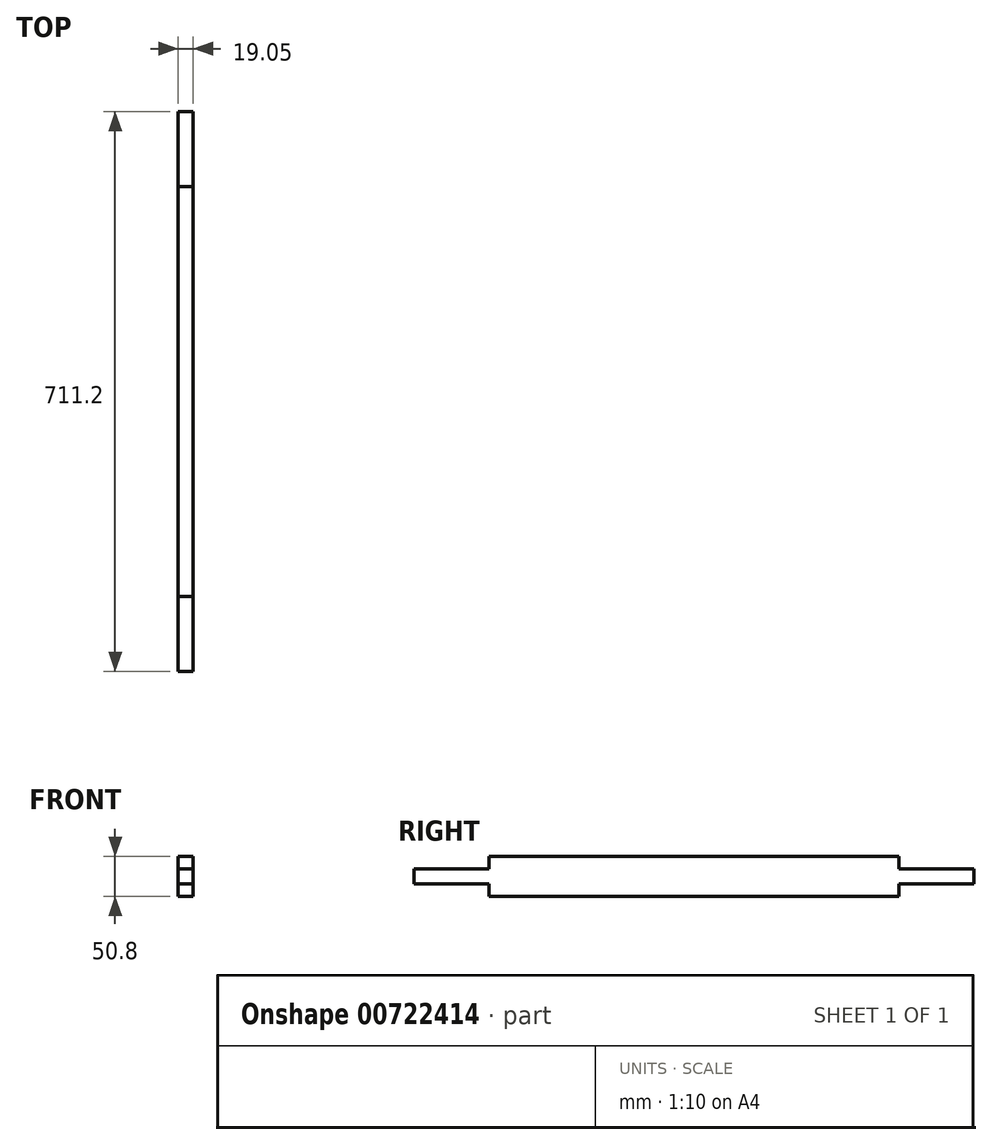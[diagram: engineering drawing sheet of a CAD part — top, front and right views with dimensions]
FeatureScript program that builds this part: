
annotation { "Feature Type Name" : "Feature", "Feature Type Description" : "" }
export const myFeature = defineFeature(function(context is Context, id is Id, definition is map)
    precondition{}
    {
        {
            var Q0;
            Q0=qCreatedBy(makeId("Right.planeOp"),FACE);
            var sketch = newSketch(context, id + "F0", { "sketchPlane" : qUnion([Q0])});
            skLineSegment(sketch, "E0.bottom", {"start": v(355.6, -25.4) * mm, "end": v(-355.6, -25.4) * mm});
            skLineSegment(sketch, "E0.top", {"start": v(355.6, 25.4) * mm, "end": v(-355.6, 25.4) * mm});
            skLineSegment(sketch, "E0.left", {"start": v(355.6, -25.4) * mm, "end": v(355.6, 25.4) * mm});
            skLineSegment(sketch, "E0.right", {"start": v(-355.6, -25.4) * mm, "end": v(-355.6, 25.4) * mm});
            skPoint(sketch, "E0.middle", {"position": v(0, 0) * mm});
            skLineSegment(sketch, "E1.bottom", {"start": v(-355.6, 25.4) * mm, "end": v(-260.35, 25.4) * mm});
            skLineSegment(sketch, "E1.top", {"start": v(-355.6, 9.52) * mm, "end": v(-260.35, 9.52) * mm});
            skLineSegment(sketch, "E1.left", {"start": v(-355.6, 25.4) * mm, "end": v(-355.6, 9.52) * mm});
            skLineSegment(sketch, "E1.right", {"start": v(-260.35, 25.4) * mm, "end": v(-260.35, 9.52) * mm});
            skLineSegment(sketch, "E2.bottom", {"start": v(-355.6, -25.4) * mm, "end": v(-260.35, -25.4) * mm});
            skLineSegment(sketch, "E2.top", {"start": v(-355.6, -9.53) * mm, "end": v(-260.35, -9.53) * mm});
            skLineSegment(sketch, "E2.left", {"start": v(-355.6, -25.4) * mm, "end": v(-355.6, -9.53) * mm});
            skLineSegment(sketch, "E2.right", {"start": v(-260.35, -25.4) * mm, "end": v(-260.35, -9.53) * mm});
            skLineSegment(sketch, "E3.bottom", {"start": v(260.35, -9.53) * mm, "end": v(355.6, -9.53) * mm});
            skLineSegment(sketch, "E3.top", {"start": v(260.35, -25.4) * mm, "end": v(355.6, -25.4) * mm});
            skLineSegment(sketch, "E3.left", {"start": v(260.35, -9.53) * mm, "end": v(260.35, -25.4) * mm});
            skLineSegment(sketch, "E3.right", {"start": v(355.6, -9.53) * mm, "end": v(355.6, -25.4) * mm});
            skLineSegment(sketch, "E4.bottom", {"start": v(355.6, 25.4) * mm, "end": v(260.35, 25.4) * mm});
            skLineSegment(sketch, "E4.top", {"start": v(355.6, 9.53) * mm, "end": v(260.35, 9.52) * mm});
            skLineSegment(sketch, "E4.left", {"start": v(355.6, 25.4) * mm, "end": v(355.6, 9.53) * mm});
            skLineSegment(sketch, "E4.right", {"start": v(260.35, 25.4) * mm, "end": v(260.35, 9.52) * mm});
            skSolve(sketch);
        }
        {
            var Q0;
            {var subQ3=sQuery(id+"F0.wireOp",EDGE,"E1.top");Q0=makeQuery(id+"F0.imprint","IMPRINT",FACE,{"disambiguationData":[TD([[makeQuery(id+"F0.imprint","IMPRINT",EDGE,{"derivedFrom":subQ3}),-1.0]])]});}
            extrude(context, id + "F1", {"entities" : qUnion([Q0]), "depth" : 19.05 * mm, "offsetDistance" : 25.4 * mm});
        }
    });
